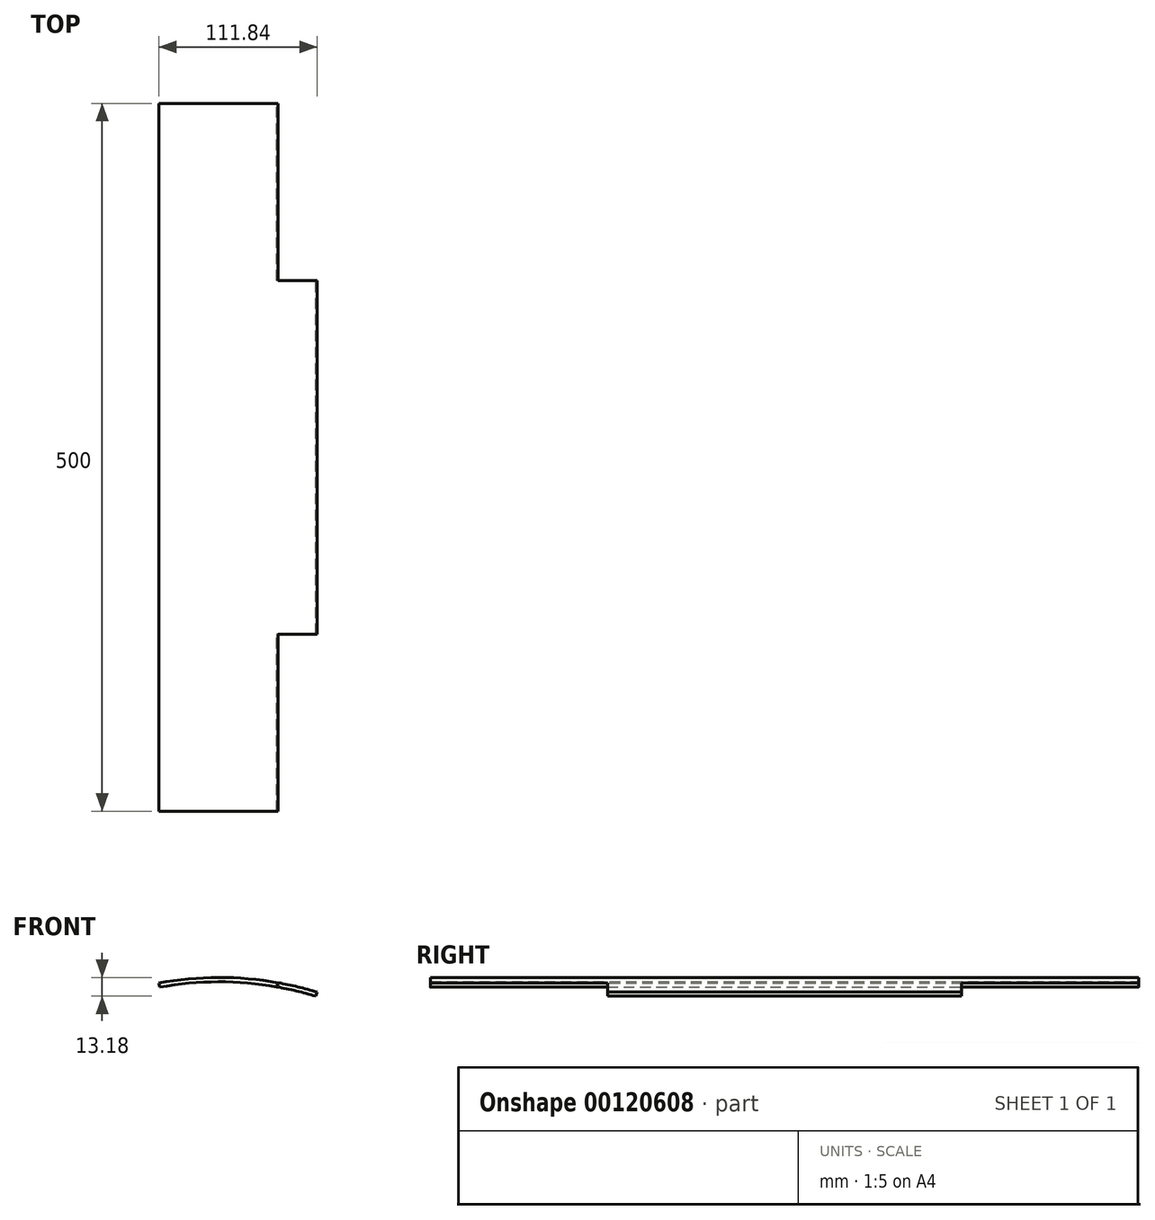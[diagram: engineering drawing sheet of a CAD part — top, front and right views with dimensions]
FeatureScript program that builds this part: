
annotation { "Feature Type Name" : "Feature", "Feature Type Description" : "" }
export const myFeature = defineFeature(function(context is Context, id is Id, definition is map)
    precondition{}
    {
        {
            var Q0;
            Q0=qCreatedBy(makeId("Front.planeOp"),FACE);
            var sketch = newSketch(context, id + "F0", { "sketchPlane" : qUnion([Q0])});
            skArc(sketch, "E0", {"start": v(14.04, -0.19) * mm, "mid": v(-41.49, 9.77) * mm, "end": v(-97.8, 6.26) * mm});
            skArc(sketch, "E1.0", {"start": v(13, -3) * mm, "mid": v(-41.62, 6.78) * mm, "end": v(-97, 3.36) * mm});
            skLineSegment(sketch, "E2", {"start": v(-97.8, 6.26) * mm, "end": v(-97, 3.36) * mm});
            skLineSegment(sketch, "E3", {"start": v(13, -3) * mm, "end": v(14.04, -0.19) * mm});
            skLineSegment(sketch, "E4", {"start": v(-13.46, 6.47) * mm, "end": v(-14.5, 3.6) * mm});
            skSolve(sketch);
        }
        {
            var Q0;
            {var subQ0=sQuery(id+"F0.wireOp",EDGE,"E2");Q0=makeQuery(id+"F0.imprint","IMPRINT",FACE,{"disambiguationData":[TD([[makeQuery(id+"F0.imprint","IMPRINT",EDGE,{"derivedFrom":subQ0}),1.0]])]});}
            extrude(context, id + "F1", {"entities" : qUnion([Q0]), "endBound" : BoundingType.SYMMETRIC, "depth" : 500 * mm});
        }
        {
            var Q0;
            {var subQ0=sQuery(id+"F0.wireOp",EDGE,"E3");Q0=makeQuery(id+"F0.imprint","IMPRINT",FACE,{"disambiguationData":[TD([[makeQuery(id+"F0.imprint","IMPRINT",EDGE,{"derivedFrom":subQ0}),1.0]])]});}
            extrude(context, id + "F2", {"entities" : qUnion([Q0]), "operationType" : NewBodyOperationType.ADD, "endBound" : BoundingType.SYMMETRIC, "depth" : 250 * mm});
        }
    });
